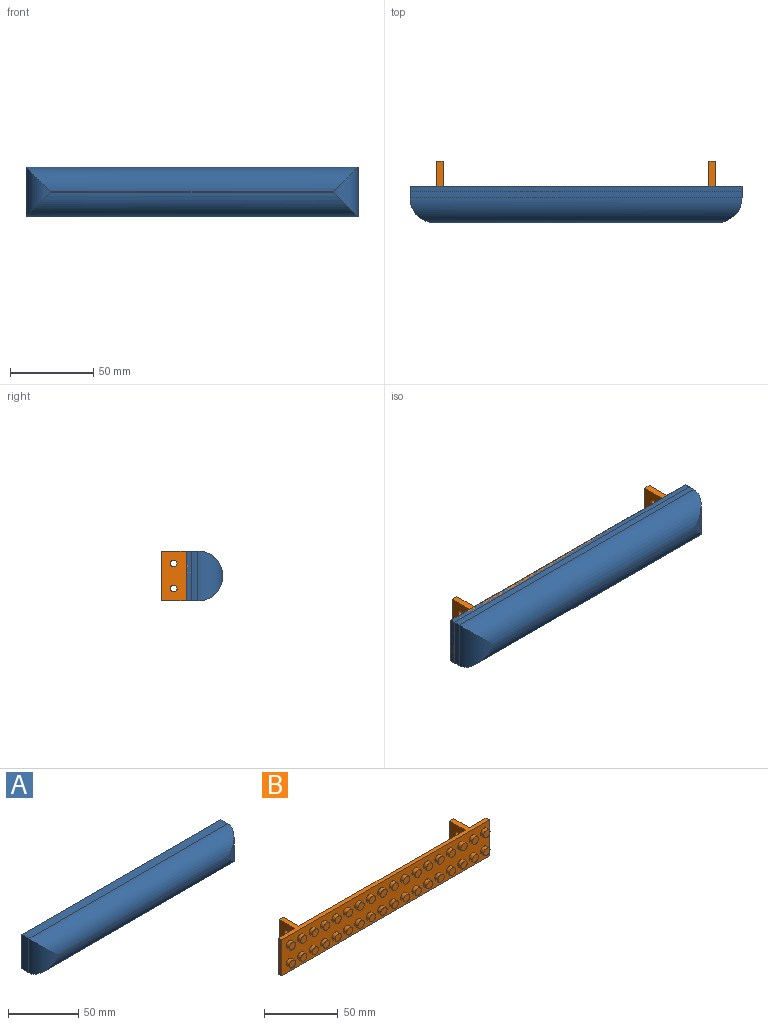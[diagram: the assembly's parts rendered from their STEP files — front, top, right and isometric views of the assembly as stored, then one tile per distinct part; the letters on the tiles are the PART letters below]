
ASSEMBLY  parts=2 mates=1
PART A: 10 faces, bbox 200x22x30 mm
  f0: plane 200x7.03mm, normal (0,0,-1), area 1406.4mm2, adj f1,f3,f5,f6
  f1: plane 30x7.03mm, normal (1,0,0), area 211mm2, adj f0,f2,f5,f7
  f2: plane 200x7.03mm, normal (0,0,1), area 1406.4mm2, adj f1,f3,f5,f9
  f3: plane 30x7.03mm, normal (-1,0,0), area 211mm2, adj f0,f2,f5,f8
  f4: plane 170.06x0.06mm, normal (0,-1,0), area 10.8mm2, adj f6,f7,f8,f9
  f5: plane 200x30mm, normal (0,1,0), area 6000mm2, adj f0,f1,f2,f3
  f6: cylinder r=14.97mm len=200mm, axis (-1,0,0), area 4446.6mm2, adj f0,f4,f7,f8
  f7: cylinder r=14.97mm len=30mm, axis (0,0,-1), area 449.6mm2, adj f1,f4,f6,f9
  f8: cylinder r=14.97mm len=30mm, axis (0,0,1), area 449.6mm2, adj f3,f4,f6,f9
  f9: cylinder r=14.97mm len=200mm, axis (1,0,0), area 4446.6mm2, adj f2,f4,f7,f8
PART B: 90 faces, bbox 200x21x30 mm
  f0: plane 30x16mm, normal (0,1,0), area 480mm2, adj f3,f5,f6,f89
  f1: plane 160x30mm, normal (0,1,0), area 4800mm2, adj f3,f5,f83,f88
  f2: plane 200x30mm, normal (0,-1,0), area 4982.1mm2, adj f3,f4,f5,f6,f8,f10,f12,f14
  f3: plane 200x18mm, normal (0,0,-1), area 720mm2, adj f0,f1,f2,f4,f6,f7,f82,f83
  f4: plane 30x3mm, normal (1,0,0), area 90mm2, adj f2,f3,f5,f7
  f5: plane 200x18mm, normal (0,0,1), area 720mm2, adj f0,f1,f2,f4,f6,f7,f82,f83
  f6: plane 30x3mm, normal (-1,0,0), area 90mm2, adj f0,f2,f3,f5
  f7: plane 30x16mm, normal (0,1,0), area 480mm2, adj f3,f4,f5,f84
  f8: cylinder r=3mm len=6mm, axis (0,1,0), area 56.5mm2, adj f2,f9
  f9: plane 6x6mm, normal (0,-1,0), area 28.3mm2, adj f8
  f10: cylinder r=3mm len=6mm, axis (0,1,0), area 56.5mm2, adj f2,f11
  f11: plane 6x6mm, normal (0,-1,0), area 28.3mm2, adj f10
  f12: cylinder r=3mm len=6mm, axis (0,1,0), area 56.5mm2, adj f2,f13
  f13: plane 6x6mm, normal (0,-1,0), area 28.3mm2, adj f12
  f14: cylinder r=3mm len=6mm, axis (0,1,0), area 56.5mm2, adj f2,f15
  f15: plane 6x6mm, normal (0,-1,0), area 28.3mm2, adj f14
  f16: cylinder r=3mm len=6mm, axis (0,1,0), area 56.5mm2, adj f2,f17
  f17: plane 6x6mm, normal (0,-1,0), area 28.3mm2, adj f16
  f18: cylinder r=3mm len=6mm, axis (0,1,0), area 56.5mm2, adj f2,f19
  f19: plane 6x6mm, normal (0,-1,0), area 28.3mm2, adj f18
  f20: cylinder r=3mm len=6mm, axis (0,1,0), area 56.5mm2, adj f2,f21
  f21: plane 6x6mm, normal (0,-1,0), area 28.3mm2, adj f20
  f22: cylinder r=3mm len=6mm, axis (0,1,0), area 56.5mm2, adj f2,f23
  f23: plane 6x6mm, normal (0,-1,0), area 28.3mm2, adj f22
  f24: cylinder r=3mm len=6mm, axis (0,1,0), area 56.5mm2, adj f2,f25
  f25: plane 6x6mm, normal (0,-1,0), area 28.3mm2, adj f24
  f26: cylinder r=3mm len=6mm, axis (0,1,0), area 56.5mm2, adj f2,f27
  f27: plane 6x6mm, normal (0,-1,0), area 28.3mm2, adj f26
  f28: cylinder r=3mm len=6mm, axis (0,1,0), area 56.5mm2, adj f2,f29
  f29: plane 6x6mm, normal (0,-1,0), area 28.3mm2, adj f28
  f30: cylinder r=3mm len=6mm, axis (0,1,0), area 56.5mm2, adj f2,f31
  f31: plane 6x6mm, normal (0,-1,0), area 28.3mm2, adj f30
  f32: cylinder r=3mm len=6mm, axis (0,1,0), area 56.5mm2, adj f2,f33
  f33: plane 6x6mm, normal (0,-1,0), area 28.3mm2, adj f32
  f34: cylinder r=3mm len=6mm, axis (0,1,0), area 56.5mm2, adj f2,f35
  f35: plane 6x6mm, normal (0,-1,0), area 28.3mm2, adj f34
  f36: cylinder r=3mm len=6mm, axis (0,1,0), area 56.5mm2, adj f2,f37
  f37: plane 6x6mm, normal (0,-1,0), area 28.3mm2, adj f36
  f38: cylinder r=3mm len=6mm, axis (0,1,0), area 56.5mm2, adj f2,f39
  f39: plane 6x6mm, normal (0,-1,0), area 28.3mm2, adj f38
  f40: cylinder r=3mm len=6mm, axis (0,1,0), area 56.5mm2, adj f2,f41
  f41: plane 6x6mm, normal (0,-1,0), area 28.3mm2, adj f40
  f42: cylinder r=3mm len=6mm, axis (0,1,0), area 56.5mm2, adj f2,f43
  f43: plane 6x6mm, normal (0,-1,0), area 28.3mm2, adj f42
  f44: plane 6x6mm, normal (0,-1,0), area 28.3mm2, adj f45
  f45: cylinder r=3mm len=6mm, axis (0,1,0), area 56.5mm2, adj f2,f44
  f46: plane 6x6mm, normal (0,-1,0), area 28.3mm2, adj f47
  f47: cylinder r=3mm len=6mm, axis (0,1,0), area 56.5mm2, adj f2,f46
  f48: plane 6x6mm, normal (0,-1,0), area 28.3mm2, adj f49
  f49: cylinder r=3mm len=6mm, axis (0,1,0), area 56.5mm2, adj f2,f48
  f50: plane 6x6mm, normal (0,-1,0), area 28.3mm2, adj f51
  f51: cylinder r=3mm len=6mm, axis (0,1,0), area 56.5mm2, adj f2,f50
  f52: plane 6x6mm, normal (0,-1,0), area 28.3mm2, adj f53
  f53: cylinder r=3mm len=6mm, axis (0,1,0), area 56.5mm2, adj f2,f52
  f54: plane 6x6mm, normal (0,-1,0), area 28.3mm2, adj f55
  f55: cylinder r=3mm len=6mm, axis (0,1,0), area 56.5mm2, adj f2,f54
  f56: plane 6x6mm, normal (0,-1,0), area 28.3mm2, adj f57
  f57: cylinder r=3mm len=6mm, axis (0,1,0), area 56.5mm2, adj f2,f56
  f58: plane 6x6mm, normal (0,-1,0), area 28.3mm2, adj f59
  f59: cylinder r=3mm len=6mm, axis (0,1,0), area 56.5mm2, adj f2,f58
  f60: plane 6x6mm, normal (0,-1,0), area 28.3mm2, adj f61
  f61: cylinder r=3mm len=6mm, axis (0,1,0), area 56.5mm2, adj f2,f60
  f62: plane 6x6mm, normal (0,-1,0), area 28.3mm2, adj f63
  f63: cylinder r=3mm len=6mm, axis (0,1,0), area 56.5mm2, adj f2,f62
  f64: plane 6x6mm, normal (0,-1,0), area 28.3mm2, adj f65
  f65: cylinder r=3mm len=6mm, axis (0,1,0), area 56.5mm2, adj f2,f64
  f66: plane 6x6mm, normal (0,-1,0), area 28.3mm2, adj f67
  f67: cylinder r=3mm len=6mm, axis (0,1,0), area 56.5mm2, adj f2,f66
  f68: plane 6x6mm, normal (0,-1,0), area 28.3mm2, adj f69
  f69: cylinder r=3mm len=6mm, axis (0,1,0), area 56.5mm2, adj f2,f68
  f70: plane 6x6mm, normal (0,-1,0), area 28.3mm2, adj f71
  f71: cylinder r=3mm len=6mm, axis (0,1,0), area 56.5mm2, adj f2,f70
  f72: plane 6x6mm, normal (0,-1,0), area 28.3mm2, adj f73
  f73: cylinder r=3mm len=6mm, axis (0,1,0), area 56.5mm2, adj f2,f72
  f74: plane 6x6mm, normal (0,-1,0), area 28.3mm2, adj f75
  f75: cylinder r=3mm len=6mm, axis (0,1,0), area 56.5mm2, adj f2,f74
  f76: plane 6x6mm, normal (0,-1,0), area 28.3mm2, adj f77
  f77: cylinder r=3mm len=6mm, axis (0,1,0), area 56.5mm2, adj f2,f76
  f78: cylinder r=3mm len=6mm, axis (0,1,0), area 56.5mm2, adj f2,f79
  f79: plane 6x6mm, normal (0,-1,0), area 28.3mm2, adj f78
  f80: cylinder r=2mm len=4mm, axis (1,0,0), area 50.3mm2, adj f83,f84
  f81: cylinder r=2mm len=4mm, axis (1,0,0), area 50.3mm2, adj f83,f84
  f82: plane 30x4mm, normal (0,1,0), area 120mm2, adj f3,f5,f83,f84
  f83: plane 30x15mm, normal (-1,0,0), area 424.9mm2, adj f1,f3,f5,f80,f81,f82
  f84: plane 30x15mm, normal (1,0,0), area 424.9mm2, adj f3,f5,f7,f80,f81,f82
  f85: cylinder r=2mm len=4mm, axis (-1,0,0), area 50.3mm2, adj f88,f89
  f86: cylinder r=2mm len=4mm, axis (-1,0,0), area 50.3mm2, adj f88,f89
  f87: plane 30x4mm, normal (0,1,0), area 120mm2, adj f3,f5,f88,f89
  f88: plane 30x15mm, normal (1,0,0), area 424.9mm2, adj f1,f3,f5,f85,f86,f87
  f89: plane 30x15mm, normal (-1,0,0), area 424.9mm2, adj f0,f3,f5,f85,f86,f87
PLACE A at identity
PLACE B at identity
MATE fastened B.f1 <-> A.f5  axis (0,1,0) through (0,0,0)mm
